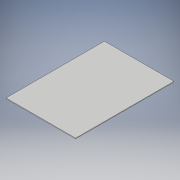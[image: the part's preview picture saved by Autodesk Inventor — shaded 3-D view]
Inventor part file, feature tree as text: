
AUTODESK INVENTOR PART (.ipt)
format: ipt  version: 2019 (Build 230136000, 136)  size: 90,624 bytes
history: native  units: mm
features: extrude x1, sketch x1
ambient origin geometry x8: Origin, YZ Plane, XZ Plane, XY Plane, X Axis, Y Axis, Z Axis, Center Point
bodies: Solid1 (feature_tree)
feature tree (2):
  extrude  "Extrusion1"  Depth=297.0mm
  sketch  "Sketch1"  dims[d0=210.0mm d1=297.0mm d2=210.0mm d3=297.0mm d4=2.0mm d5=0.0mm]
